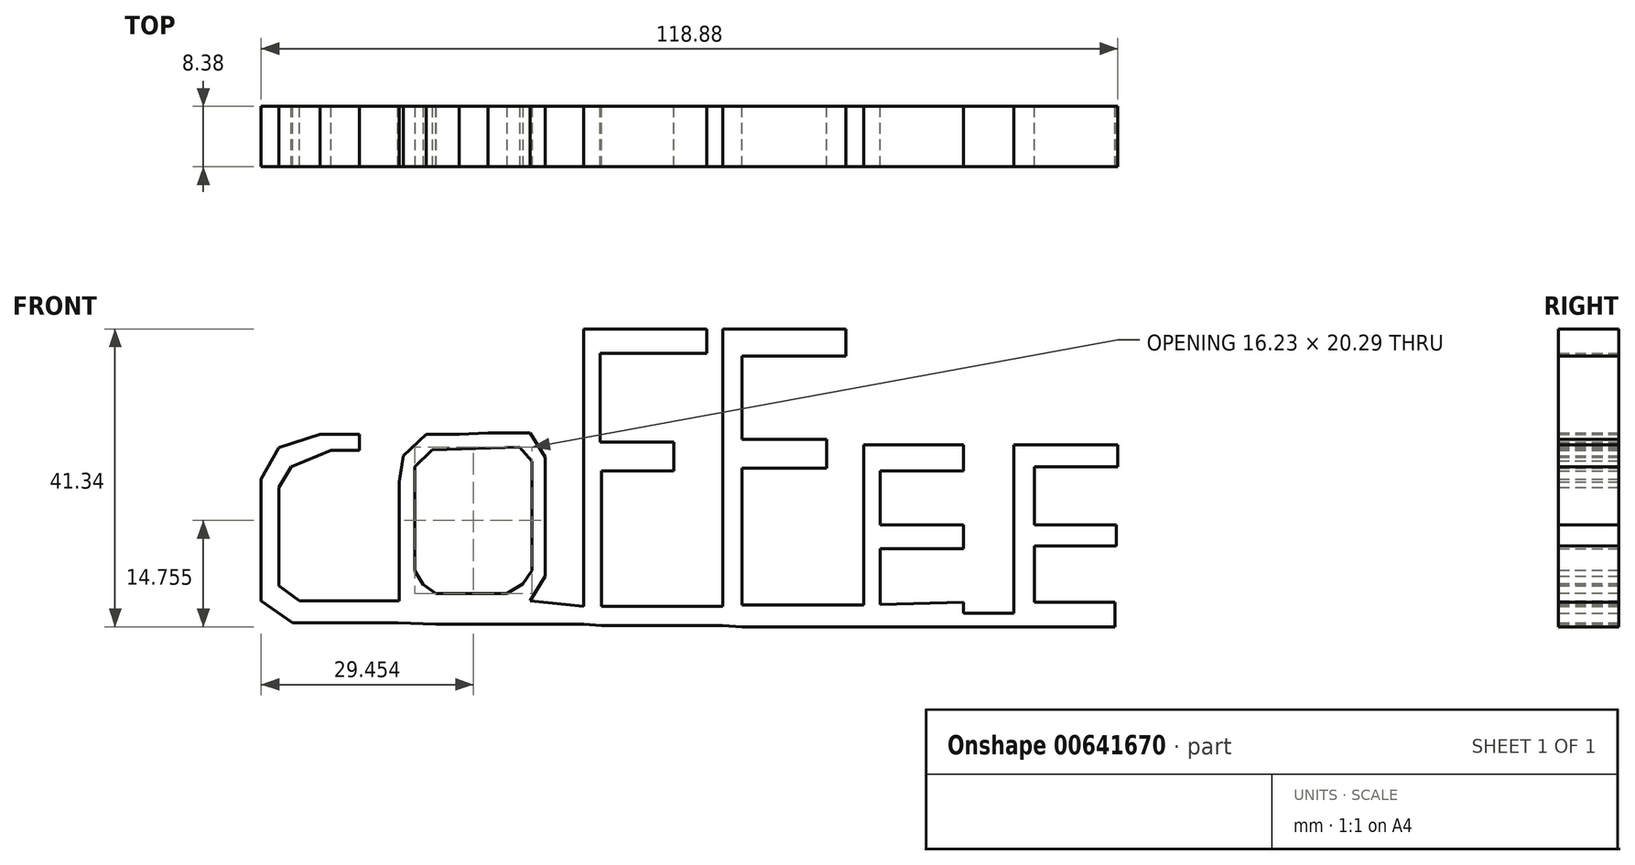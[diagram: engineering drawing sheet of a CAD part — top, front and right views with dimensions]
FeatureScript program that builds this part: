
annotation { "Feature Type Name" : "Feature", "Feature Type Description" : "" }
export const myFeature = defineFeature(function(context is Context, id is Id, definition is map)
    precondition{}
    {
        {
            var Q0;
            Q0=qCreatedBy(makeId("Front.planeOp"),FACE);
            var sketch = newSketch(context, id + "F0", { "sketchPlane" : qUnion([Q0])});
            skLineSegment(sketch, "E0", {"start": v(-41.24, 41.43) * mm, "end": v(-46.74, 41.43) * mm});
            skLineSegment(sketch, "E1", {"start": v(-46.74, 41.43) * mm, "end": v(-52.42, 39.53) * mm});
            skLineSegment(sketch, "E2", {"start": v(-52.42, 39.53) * mm, "end": v(-54.89, 35.17) * mm});
            skLineSegment(sketch, "E3", {"start": v(-54.89, 35.17) * mm, "end": v(-54.89, 26.83) * mm});
            skLineSegment(sketch, "E4", {"start": v(-54.89, 26.83) * mm, "end": v(-54.89, 18.3) * mm});
            skLineSegment(sketch, "E5", {"start": v(-54.89, 18.3) * mm, "end": v(-50.53, 15.26) * mm});
            skLineSegment(sketch, "E6", {"start": v(-50.53, 15.26) * mm, "end": v(-46.17, 15.26) * mm});
            skLineSegment(sketch, "E7", {"start": v(-46.17, 15.26) * mm, "end": v(-42, 15.26) * mm});
            skLineSegment(sketch, "E8", {"start": v(-42, 15.26) * mm, "end": v(-35.93, 15.26) * mm});
            skLineSegment(sketch, "E9", {"start": v(-41.24, 41.43) * mm, "end": v(-41.24, 39.15) * mm});
            skLineSegment(sketch, "E10", {"start": v(-41.24, 39.15) * mm, "end": v(-45.22, 39.15) * mm});
            skLineSegment(sketch, "E11", {"start": v(-45.22, 39.15) * mm, "end": v(-50.72, 36.88) * mm});
            skLineSegment(sketch, "E12", {"start": v(-50.72, 36.88) * mm, "end": v(-52.42, 34.03) * mm});
            skLineSegment(sketch, "E13", {"start": v(-52.42, 34.03) * mm, "end": v(-52.42, 25.88) * mm});
            skLineSegment(sketch, "E14", {"start": v(-52.42, 25.88) * mm, "end": v(-52.42, 20.38) * mm});
            skLineSegment(sketch, "E15", {"start": v(-52.42, 20.38) * mm, "end": v(-49.58, 18.3) * mm});
            skLineSegment(sketch, "E16", {"start": v(-49.58, 18.3) * mm, "end": v(-41.24, 18.3) * mm});
            skLineSegment(sketch, "E17", {"start": v(-41.24, 18.3) * mm, "end": v(-35.74, 18.3) * mm});
            skLineSegment(sketch, "E18", {"start": v(-35.74, 18.3) * mm, "end": v(-35.74, 34.8) * mm});
            skLineSegment(sketch, "E19", {"start": v(-35.74, 34.8) * mm, "end": v(-35.17, 38.4) * mm});
            skLineSegment(sketch, "E20", {"start": v(-35.17, 38.4) * mm, "end": v(-31.95, 41.43) * mm});
            skLineSegment(sketch, "E21", {"start": v(-31.95, 41.43) * mm, "end": v(-27.4, 41.43) * mm});
            skLineSegment(sketch, "E22", {"start": v(-27.4, 41.43) * mm, "end": v(-23.42, 41.62) * mm});
            skLineSegment(sketch, "E23", {"start": v(-23.42, 41.62) * mm, "end": v(-17.54, 41.62) * mm});
            skLineSegment(sketch, "E24", {"start": v(-17.54, 41.62) * mm, "end": v(-15.45, 38.2) * mm});
            skLineSegment(sketch, "E25", {"start": v(-15.45, 38.2) * mm, "end": v(-15.45, 32.52) * mm});
            skLineSegment(sketch, "E26", {"start": v(-15.45, 32.52) * mm, "end": v(-15.45, 21.7) * mm});
            skLineSegment(sketch, "E27", {"start": v(-15.45, 21.7) * mm, "end": v(-17.54, 18.3) * mm});
            skLineSegment(sketch, "E28", {"start": v(-17.54, 18.3) * mm, "end": v(-20.95, 15.07) * mm});
            skLineSegment(sketch, "E29", {"start": v(-20.95, 15.07) * mm, "end": v(-30.62, 15.07) * mm});
            skLineSegment(sketch, "E30", {"start": v(-30.62, 15.07) * mm, "end": v(-35.74, 18.3) * mm});
            skLineSegment(sketch, "E31", {"start": v(-35.93, 15.26) * mm, "end": v(-30.62, 15.07) * mm});
            skLineSegment(sketch, "E32", {"start": v(-20.95, 15.07) * mm, "end": v(-10.14, 15.07) * mm});
            skLineSegment(sketch, "E33", {"start": v(-10.14, 15.07) * mm, "end": v(-10.14, 17.54) * mm});
            skLineSegment(sketch, "E34", {"start": v(-10.14, 17.54) * mm, "end": v(-10.14, 56.03) * mm});
            skLineSegment(sketch, "E35", {"start": v(-10.14, 56.03) * mm, "end": v(6.92, 56.03) * mm});
            skLineSegment(sketch, "E36", {"start": v(6.92, 56.03) * mm, "end": v(6.92, 52.61) * mm});
            skLineSegment(sketch, "E37", {"start": v(6.92, 52.61) * mm, "end": v(-10.14, 52.61) * mm});
            skLineSegment(sketch, "E38", {"start": v(-10.14, 40.29) * mm, "end": v(2.37, 40.29) * mm});
            skLineSegment(sketch, "E39", {"start": v(2.37, 40.29) * mm, "end": v(2.37, 36.3) * mm});
            skLineSegment(sketch, "E40", {"start": v(2.37, 36.3) * mm, "end": v(-10.14, 36.3) * mm});
            skLineSegment(sketch, "E41", {"start": v(-7.87, 52.61) * mm, "end": v(-7.87, 40.29) * mm});
            skLineSegment(sketch, "E42", {"start": v(-7.68, 36.3) * mm, "end": v(-7.68, 14.88) * mm});
            skLineSegment(sketch, "E43", {"start": v(-7.68, 14.88) * mm, "end": v(-10.14, 15.07) * mm});
            skLineSegment(sketch, "E44", {"start": v(-7.68, 14.88) * mm, "end": v(9.2, 14.88) * mm});
            skLineSegment(sketch, "E45", {"start": v(9.2, 14.88) * mm, "end": v(9.2, 17.54) * mm});
            skLineSegment(sketch, "E46", {"start": v(9.2, 17.54) * mm, "end": v(-7.68, 17.54) * mm});
            skLineSegment(sketch, "E47", {"start": v(9.2, 17.54) * mm, "end": v(9.2, 56.03) * mm});
            skLineSegment(sketch, "E48", {"start": v(9.2, 56.03) * mm, "end": v(26.26, 56.03) * mm});
            skLineSegment(sketch, "E49", {"start": v(26.26, 56.03) * mm, "end": v(26.26, 52.23) * mm});
            skLineSegment(sketch, "E50", {"start": v(26.26, 52.23) * mm, "end": v(9.2, 52.23) * mm});
            skLineSegment(sketch, "E51", {"start": v(9.2, 40.67) * mm, "end": v(23.6, 40.67) * mm});
            skLineSegment(sketch, "E52", {"start": v(23.6, 40.67) * mm, "end": v(23.6, 36.69) * mm});
            skLineSegment(sketch, "E53", {"start": v(23.6, 36.69) * mm, "end": v(9.2, 36.69) * mm});
            skLineSegment(sketch, "E54", {"start": v(11.85, 52.23) * mm, "end": v(11.85, 40.67) * mm});
            skLineSegment(sketch, "E55", {"start": v(11.85, 40.67) * mm, "end": v(11.85, 36.69) * mm});
            skLineSegment(sketch, "E56", {"start": v(11.85, 36.69) * mm, "end": v(11.85, 14.7) * mm});
            skLineSegment(sketch, "E57", {"start": v(11.85, 14.7) * mm, "end": v(9.2, 14.88) * mm});
            skLineSegment(sketch, "E58", {"start": v(11.85, 14.7) * mm, "end": v(28.72, 14.7) * mm});
            skLineSegment(sketch, "E59", {"start": v(28.72, 14.7) * mm, "end": v(28.72, 17.73) * mm});
            skLineSegment(sketch, "E60", {"start": v(28.72, 17.73) * mm, "end": v(11.85, 17.73) * mm});
            skLineSegment(sketch, "E61", {"start": v(28.72, 17.73) * mm, "end": v(28.72, 39.91) * mm});
            skPoint(sketch, "E61.endSnap0", {"position": v(-33.56, 39.91) * mm});
            skLineSegment(sketch, "E62", {"start": v(28.72, 39.91) * mm, "end": v(42.56, 39.91) * mm});
            skLineSegment(sketch, "E63", {"start": v(42.56, 39.91) * mm, "end": v(42.56, 36.3) * mm});
            skLineSegment(sketch, "E64", {"start": v(42.56, 36.3) * mm, "end": v(28.72, 36.3) * mm});
            skLineSegment(sketch, "E65", {"start": v(28.72, 28.82) * mm, "end": v(42.56, 28.82) * mm});
            skLineSegment(sketch, "E66", {"start": v(42.56, 28.82) * mm, "end": v(42.56, 25.5) * mm});
            skLineSegment(sketch, "E67", {"start": v(42.56, 25.5) * mm, "end": v(28.72, 25.5) * mm});
            skLineSegment(sketch, "E68", {"start": v(28.72, 14.7) * mm, "end": v(42.56, 14.7) * mm});
            skLineSegment(sketch, "E69", {"start": v(42.56, 14.7) * mm, "end": v(42.56, 18.1) * mm});
            skLineSegment(sketch, "E70", {"start": v(42.56, 18.1) * mm, "end": v(28.72, 17.73) * mm});
            skLineSegment(sketch, "E71", {"start": v(31, 17.79) * mm, "end": v(31, 36.3) * mm});
            skLineSegment(sketch, "E72", {"start": v(42.56, 14.7) * mm, "end": v(49.58, 14.7) * mm});
            skLineSegment(sketch, "E73", {"start": v(49.58, 14.7) * mm, "end": v(49.58, 16.59) * mm});
            skLineSegment(sketch, "E74", {"start": v(49.58, 16.59) * mm, "end": v(42.56, 16.59) * mm});
            skLineSegment(sketch, "E75", {"start": v(49.58, 16.59) * mm, "end": v(49.58, 39.91) * mm});
            skLineSegment(sketch, "E76", {"start": v(49.58, 39.91) * mm, "end": v(63.99, 39.91) * mm});
            skLineSegment(sketch, "E77", {"start": v(63.99, 39.91) * mm, "end": v(63.99, 36.88) * mm});
            skLineSegment(sketch, "E78", {"start": v(63.99, 36.88) * mm, "end": v(49.58, 36.88) * mm});
            skLineSegment(sketch, "E79", {"start": v(49.58, 28.82) * mm, "end": v(63.8, 28.82) * mm});
            skPoint(sketch, "E79.startSnap0", {"position": v(49.58, 28.25) * mm});
            skLineSegment(sketch, "E80", {"start": v(63.8, 28.82) * mm, "end": v(63.8, 25.88) * mm});
            skLineSegment(sketch, "E81", {"start": v(63.8, 25.88) * mm, "end": v(49.58, 25.88) * mm});
            skLineSegment(sketch, "E82", {"start": v(49.58, 14.7) * mm, "end": v(63.6, 14.7) * mm});
            skLineSegment(sketch, "E83", {"start": v(63.6, 14.7) * mm, "end": v(63.6, 18.1) * mm});
            skLineSegment(sketch, "E84", {"start": v(63.6, 18.1) * mm, "end": v(49.58, 18.1) * mm});
            skLineSegment(sketch, "E85", {"start": v(-17.54, 17.54) * mm, "end": v(-20.95, 15.07) * mm});
            skLineSegment(sketch, "E86", {"start": v(-17.54, 18.3) * mm, "end": v(-10.14, 17.54) * mm});
            skLineSegment(sketch, "E87", {"start": v(52.42, 36.88) * mm, "end": v(52.42, 18.1) * mm});
            skSolve(sketch);
        }
        {
            var Q0;
            Q0 = qSketchRegion(id + "F0", true);
            extrude(context, id + "F1", {"entities" : qUnion([Q0]), "depth" : 7.62 * mm, "offsetDistance" : 25.4 * mm});
        }
        {
            var Q0;
            Q0 = qSketchRegion(id + "F0", true);
            extrude(context, id + "F2", {"entities" : qUnion([Q0]), "operationType" : NewBodyOperationType.ADD, "depth" : 8.38 * mm, "offsetDistance" : 25.4 * mm});
        }
        {
            var Q0;
            Q0=makeQuery(id+"F2.opExtrude","CAP_FACE",FACE,{"disambiguationData":[OSD([sQuery(id+"F0.wireOp",EDGE,"E0"),sQuery(id+"F0.wireOp",EDGE,"E1"),sQuery(id+"F0.wireOp",EDGE,"E2"),sQuery(id+"F0.wireOp",EDGE,"E3"),sQuery(id+"F0.wireOp",EDGE,"E4"),sQuery(id+"F0.wireOp",EDGE,"E5"),sQuery(id+"F0.wireOp",EDGE,"E6"),sQuery(id+"F0.wireOp",EDGE,"E7"),sQuery(id+"F0.wireOp",EDGE,"E8"),sQuery(id+"F0.wireOp",EDGE,"E9"),sQuery(id+"F0.wireOp",EDGE,"E10"),sQuery(id+"F0.wireOp",EDGE,"E11"),sQuery(id+"F0.wireOp",EDGE,"E12"),sQuery(id+"F0.wireOp",EDGE,"E13"),sQuery(id+"F0.wireOp",EDGE,"E14"),sQuery(id+"F0.wireOp",EDGE,"E15"),sQuery(id+"F0.wireOp",EDGE,"E16"),sQuery(id+"F0.wireOp",EDGE,"E17"),sQuery(id+"F0.wireOp",EDGE,"E18"),sQuery(id+"F0.wireOp",EDGE,"E19"),sQuery(id+"F0.wireOp",EDGE,"E20"),sQuery(id+"F0.wireOp",EDGE,"E21"),sQuery(id+"F0.wireOp",EDGE,"E22"),sQuery(id+"F0.wireOp",EDGE,"E23"),sQuery(id+"F0.wireOp",EDGE,"E24"),sQuery(id+"F0.wireOp",EDGE,"E25"),sQuery(id+"F0.wireOp",EDGE,"E26"),sQuery(id+"F0.wireOp",EDGE,"E27"),sQuery(id+"F0.wireOp",EDGE,"E29"),sQuery(id+"F0.wireOp",EDGE,"E31"),sQuery(id+"F0.wireOp",EDGE,"E32"),sQuery(id+"F0.wireOp",EDGE,"E34"),sQuery(id+"F0.wireOp",EDGE,"E35"),sQuery(id+"F0.wireOp",EDGE,"E36"),sQuery(id+"F0.wireOp",EDGE,"E37"),sQuery(id+"F0.wireOp",EDGE,"E38"),sQuery(id+"F0.wireOp",EDGE,"E39"),sQuery(id+"F0.wireOp",EDGE,"E40"),sQuery(id+"F0.wireOp",EDGE,"E41"),sQuery(id+"F0.wireOp",EDGE,"E42"),sQuery(id+"F0.wireOp",EDGE,"E43"),sQuery(id+"F0.wireOp",EDGE,"E44"),sQuery(id+"F0.wireOp",EDGE,"E46"),sQuery(id+"F0.wireOp",EDGE,"E47"),sQuery(id+"F0.wireOp",EDGE,"E48"),sQuery(id+"F0.wireOp",EDGE,"E49"),sQuery(id+"F0.wireOp",EDGE,"E50"),sQuery(id+"F0.wireOp",EDGE,"E51"),sQuery(id+"F0.wireOp",EDGE,"E52"),sQuery(id+"F0.wireOp",EDGE,"E53"),sQuery(id+"F0.wireOp",EDGE,"E54"),sQuery(id+"F0.wireOp",EDGE,"E56"),sQuery(id+"F0.wireOp",EDGE,"E57"),sQuery(id+"F0.wireOp",EDGE,"E58"),sQuery(id+"F0.wireOp",EDGE,"E60"),sQuery(id+"F0.wireOp",EDGE,"E61"),sQuery(id+"F0.wireOp",EDGE,"E62"),sQuery(id+"F0.wireOp",EDGE,"E63"),sQuery(id+"F0.wireOp",EDGE,"E64"),sQuery(id+"F0.wireOp",EDGE,"E65"),sQuery(id+"F0.wireOp",EDGE,"E66"),sQuery(id+"F0.wireOp",EDGE,"E67"),sQuery(id+"F0.wireOp",EDGE,"E68"),sQuery(id+"F0.wireOp",EDGE,"E69"),sQuery(id+"F0.wireOp",EDGE,"E70"),sQuery(id+"F0.wireOp",EDGE,"E71"),sQuery(id+"F0.wireOp",EDGE,"E72"),sQuery(id+"F0.wireOp",EDGE,"E74"),sQuery(id+"F0.wireOp",EDGE,"E75"),sQuery(id+"F0.wireOp",EDGE,"E76"),sQuery(id+"F0.wireOp",EDGE,"E77"),sQuery(id+"F0.wireOp",EDGE,"E78"),sQuery(id+"F0.wireOp",EDGE,"E79"),sQuery(id+"F0.wireOp",EDGE,"E80"),sQuery(id+"F0.wireOp",EDGE,"E81"),sQuery(id+"F0.wireOp",EDGE,"E82"),sQuery(id+"F0.wireOp",EDGE,"E83"),sQuery(id+"F0.wireOp",EDGE,"E84"),sQuery(id+"F0.wireOp",EDGE,"E86"),sQuery(id+"F0.wireOp",EDGE,"E87")])],"isStart":false});
            var sketch = newSketch(context, id + "F3", { "sketchPlane" : qUnion([Q0])});
            skLineSegment(sketch, "E88", {"start": v(-31.19, 39.25) * mm, "end": v(-33.55, 36.89) * mm});
            skLineSegment(sketch, "E89", {"start": v(-33.55, 36.89) * mm, "end": v(-33.55, 32.83) * mm});
            skLineSegment(sketch, "E90", {"start": v(-33.55, 32.83) * mm, "end": v(-33.55, 22.46) * mm});
            skLineSegment(sketch, "E91", {"start": v(-33.55, 22.46) * mm, "end": v(-32.43, 20.54) * mm});
            skLineSegment(sketch, "E92", {"start": v(-32.43, 20.54) * mm, "end": v(-30.62, 19.3) * mm});
            skLineSegment(sketch, "E93", {"start": v(-30.62, 19.3) * mm, "end": v(-20.81, 19.3) * mm});
            skLineSegment(sketch, "E94", {"start": v(-20.81, 19.3) * mm, "end": v(-18.56, 20.65) * mm});
            skLineSegment(sketch, "E95", {"start": v(-18.56, 20.65) * mm, "end": v(-17.32, 22.46) * mm});
            skLineSegment(sketch, "E96", {"start": v(-17.32, 22.46) * mm, "end": v(-17.32, 32.83) * mm});
            skLineSegment(sketch, "E97", {"start": v(-17.32, 32.83) * mm, "end": v(-17.32, 37.68) * mm});
            skLineSegment(sketch, "E98", {"start": v(-17.32, 37.68) * mm, "end": v(-19.01, 39.6) * mm});
            skLineSegment(sketch, "E99", {"start": v(-19.01, 39.6) * mm, "end": v(-31.19, 39.25) * mm});
            skSolve(sketch);
        }
        {
            var Q0;
            Q0 = qSketchRegion(id + "F3", true);
            extrude(context, id + "F4", {"entities" : qUnion([Q0]), "operationType" : NewBodyOperationType.REMOVE, "oppositeDirection" : true, "depth" : 25.4 * mm, "offsetDistance" : 25.4 * mm});
        }
    });
